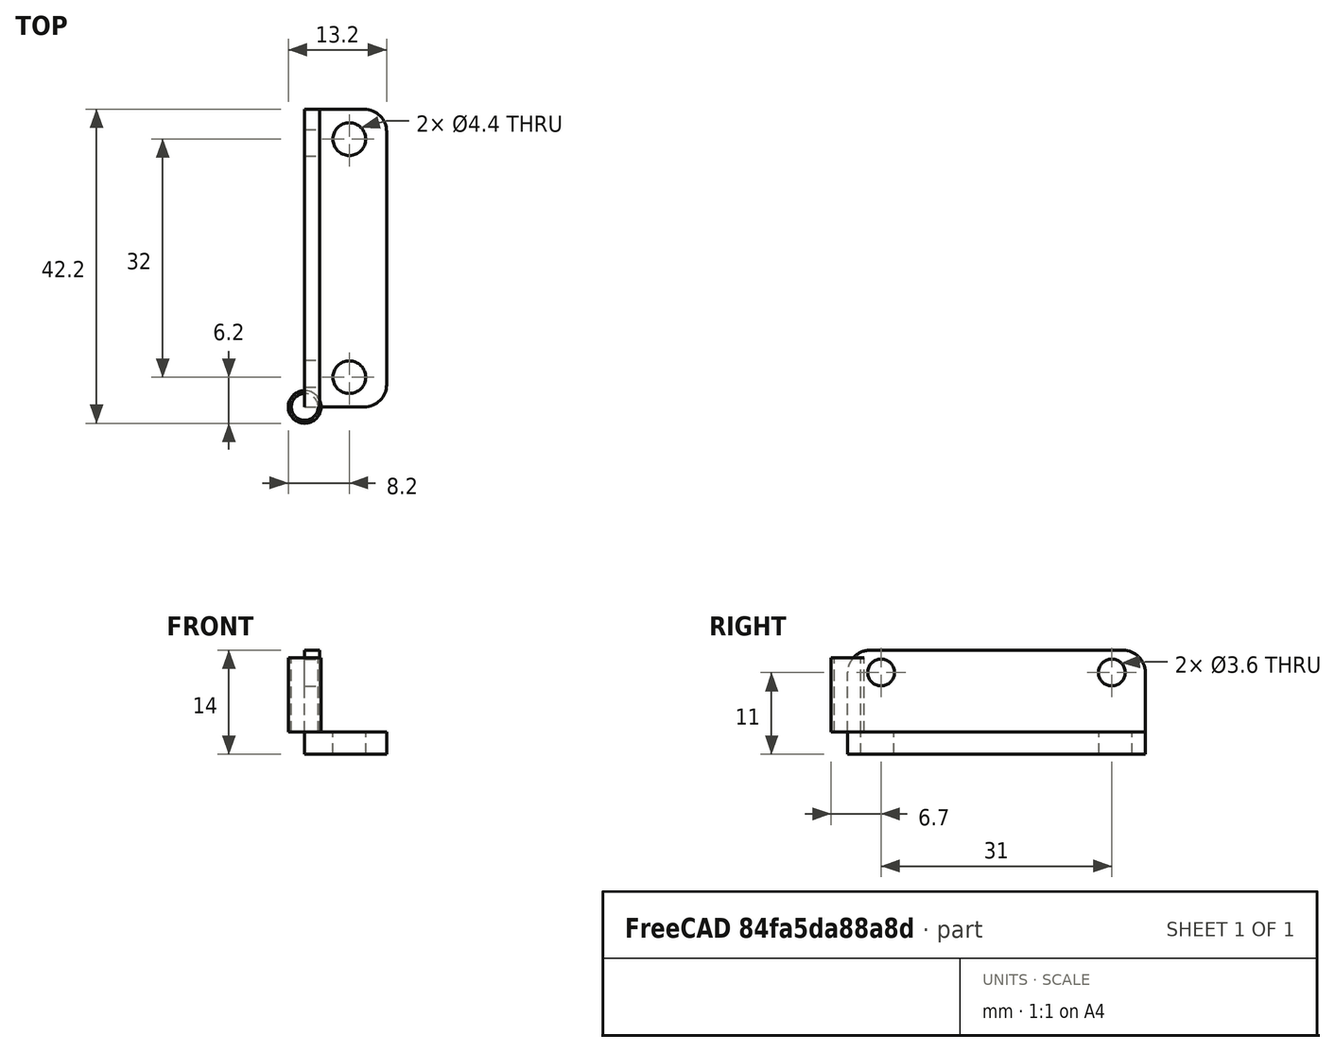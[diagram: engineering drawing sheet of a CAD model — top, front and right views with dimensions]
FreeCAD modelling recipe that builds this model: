
FCSTD DOCUMENT  (FreeCAD 0.19R)
Label: stepper_pcb_holder
License: All rights reserved
LicenseURL: http://en.wikipedia.org/wiki/All_rights_reserved
objects: Part::Box×2, Part::Cylinder×2, Part::FeaturePython×2, Part::MultiFuse×2, Part::Fillet×2, Part::Cut×1
note: 9 computed .brp shape members not serialized (recipe doc carries the construction recipe); baked Part::Feature solids carry a one-line shape summary decoded from their .brp

FEATURE [Part::Box] Box  label="top cube"
  AttacherType = Attacher::AttachEngine3D
  Height = 3
  Length = 11
  Placement = pos=(0,0,-3) rot=(0,0,1;0rad)
  Width = 40
  expr: .Placement.Base.z = -Height
FEATURE [Part::Box] Box001  label="stepper cube"
  AttacherType = Attacher::AttachEngine3D
  Height = 11
  Length = 2
  Width = 40
  expr: Width = <<top cube>>.Width
FEATURE [Part::Cylinder] Cylinder
  Angle = 360
  AttacherType = Attacher::AttachEngine3D
  Height = 10
  Radius = 1.8
FEATURE [Part::FeaturePython] Array  label="stepper hole array"  # Draft array (typed FeaturePython)
  Angle = 360
  ArrayType = 0
  Axis = (0,0,1)
  Base = -> Cylinder
  Center = (0,0,0)
  Count = 2
  ExpandArray = false
  Fuse = false
  IntervalAxis = (0,0,0)
  IntervalX = (100,0,0)
  IntervalY = (0,31,0)
  IntervalZ = (0,0,100)
  NumberCircles = 3
  NumberPolar = 5
  NumberX = 1
  NumberY = 2
  NumberZ = 1
  Placement = pos=(0,4.5,8) rot=(0,1,0;1.5708rad)
  PlacementList = 2 placements: [(0,0,0),(0,31,0)]
  RadialDistance = 50
  ScaleList = (2) [(1,1,1),(1,1,1)]
  Symmetry = 1
  TangentialDistance = 25
  expr: .Placement.Base.y = (<<top cube>>.Width - .IntervalY.y) / 2
FEATURE [Part::Cylinder] Cylinder001
  Angle = 360
  AttacherType = Attacher::AttachEngine3D
  Height = 10
  Radius = 2.2
FEATURE [Part::FeaturePython] Array001  label="pcb hole array"  # Draft array (typed FeaturePython)
  Angle = 360
  ArrayType = 0
  Axis = (0,0,1)
  Base = -> Cylinder001
  Center = (0,0,0)
  Count = 2
  ExpandArray = false
  Fuse = false
  IntervalAxis = (0,0,0)
  IntervalX = (100,0,0)
  IntervalY = (0,32,0)
  IntervalZ = (0,0,100)
  NumberCircles = 3
  NumberPolar = 5
  NumberX = 1
  NumberY = 2
  NumberZ = 1
  Placement = pos=(6,4,-3) rot=(0,1,0;0rad)
  PlacementList = 2 placements: [(0,0,0),(0,32,0)]
  RadialDistance = 50
  ScaleList = (2) [(1,1,1),(1,1,1)]
  Symmetry = 1
  TangentialDistance = 25
  expr: .Placement.Base.z = -<<top cube>>.Height
  expr: .Placement.Base.y = (<<top cube>>.Width - .IntervalY.y) / 2
FEATURE [Part::MultiFuse] Fusion
  Shapes = -> [Array,Array001]
FEATURE [Part::Fillet] Fillet
  Base = -> Box
  Edges = 2 edges r=3: [Edge5,Edge7]
FEATURE [Part::Fillet] Fillet001
  Base = -> Box001
  Edges = 2 edges r=3: [Edge10,Edge12]
FEATURE [Part::MultiFuse] Fusion001
  Shapes = -> [Fillet,Fillet001]
FEATURE [Part::Cut] Cut
  Base = -> Fusion001
  Tool = -> Fusion
